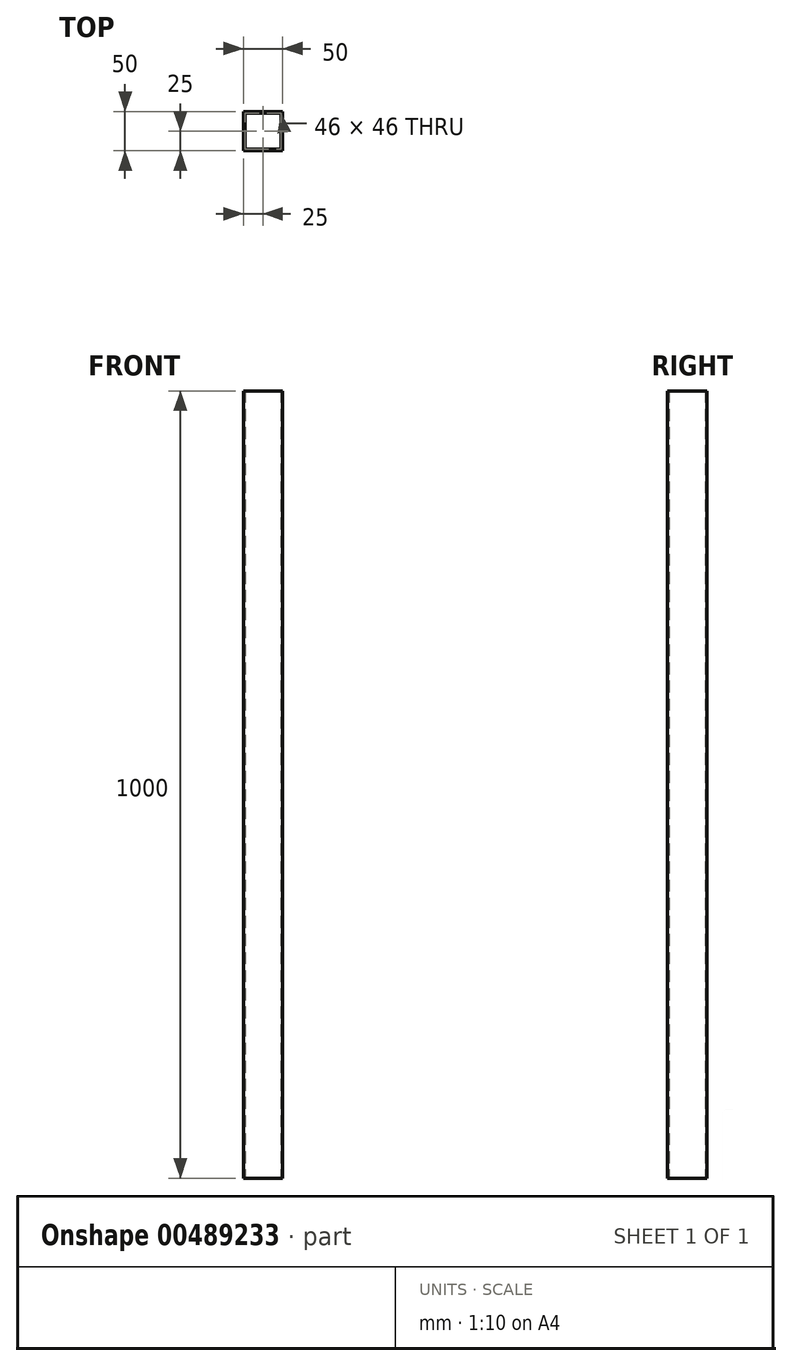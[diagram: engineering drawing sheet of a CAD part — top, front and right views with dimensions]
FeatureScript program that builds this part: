
annotation { "Feature Type Name" : "Feature", "Feature Type Description" : "" }
export const myFeature = defineFeature(function(context is Context, id is Id, definition is map)
    precondition{}
    {
        {
            var Q0;
            Q0=qCreatedBy(makeId("Top.planeOp"),FACE);
            var sketch = newSketch(context, id + "F0", { "sketchPlane" : qUnion([Q0])});
            skLineSegment(sketch, "E0.bottom", {"start": v(0, 0) * mm, "end": v(50, 0) * mm});
            skLineSegment(sketch, "E0.top", {"start": v(0, -50) * mm, "end": v(50, -50) * mm});
            skLineSegment(sketch, "E0.left", {"start": v(0, 0) * mm, "end": v(0, -50) * mm});
            skLineSegment(sketch, "E0.right", {"start": v(50, 0) * mm, "end": v(50, -50) * mm});
            skLineSegment(sketch, "E1.0", {"start": v(48, -2) * mm, "end": v(48, -48) * mm});
            skLineSegment(sketch, "E1.1", {"start": v(2, -2) * mm, "end": v(48, -2) * mm});
            skLineSegment(sketch, "E1.2", {"start": v(2, -2) * mm, "end": v(2, -48) * mm});
            skLineSegment(sketch, "E1.3", {"start": v(2, -48) * mm, "end": v(48, -48) * mm});
            skSolve(sketch);
        }
        {
            var Q0;
            Q0 = qSketchRegion(id + "F0", true);
            extrude(context, id + "F1", {"entities" : qUnion([Q0]), "depth" : 1000 * mm});
        }
    });
